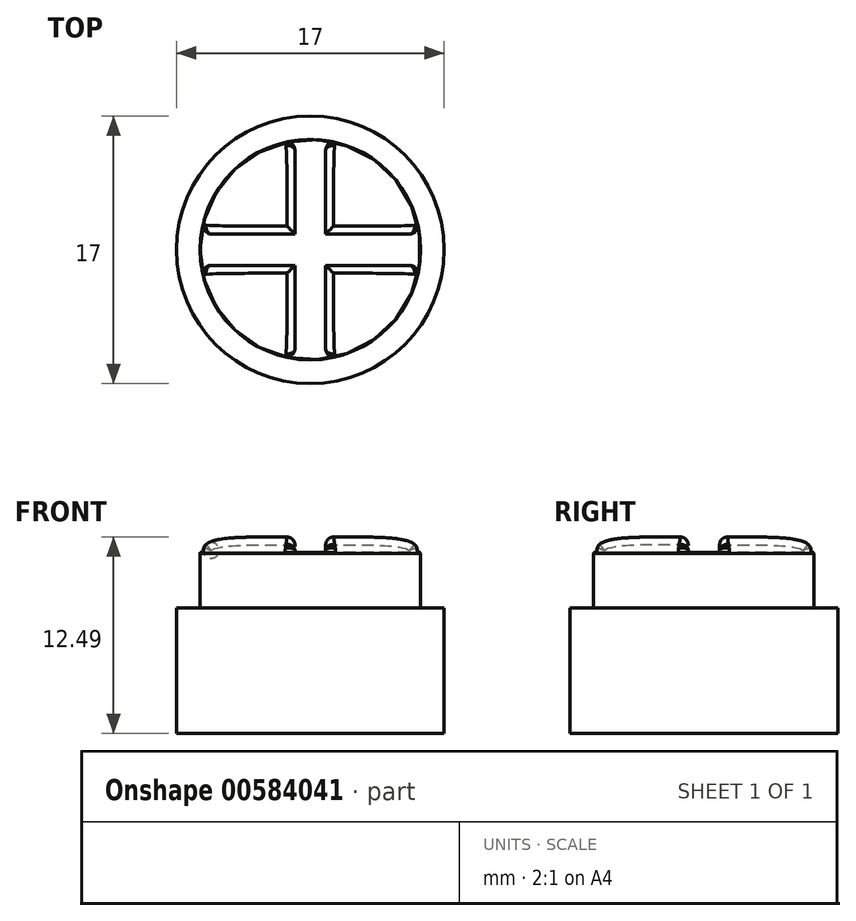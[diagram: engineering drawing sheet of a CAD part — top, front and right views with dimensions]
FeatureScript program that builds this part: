
annotation { "Feature Type Name" : "Feature", "Feature Type Description" : "" }
export const myFeature = defineFeature(function(context is Context, id is Id, definition is map)
    precondition{}
    {
        {
            var Q0;
            Q0=qCreatedBy(makeId("Top.planeOp"),FACE);
            var sketch = newSketch(context, id + "F0", { "sketchPlane" : qUnion([Q0])});
            skCircle(sketch, "E0", {"center": v(0, 0) * mm, "radius": 7 * mm});
            skCircle(sketch, "E1", {"center": v(0, 0) * mm, "radius": 8.5 * mm});
            skSolve(sketch);
        }
        {
            var Q0;
            Q0=makeQuery(id+"F0.imprint","IMPRINT",FACE,{"disambiguationData":[TD([[makeQuery(id+"F0.imprint","IMPRINT",EDGE,{"derivedFrom":sQuery(id+"F0.wireOp",EDGE,"E0")}),1.0]])]});
            extrude(context, id + "F1", {"entities" : qUnion([Q0]), "depth" : 12.5 * mm, "offsetDistance" : 25 * mm});
        }
        {
            var Q0;
            Q0 = qSketchRegion(id + "F0", true);
            extrude(context, id + "F2", {"entities" : qUnion([Q0]), "operationType" : NewBodyOperationType.ADD, "depth" : 8 * mm, "offsetDistance" : 25 * mm});
        }
        {
            var Q0;
            Q0=makeQuery(id+"F1.opExtrude","CAP_FACE",FACE,{"disambiguationData":[OSD([sQuery(id+"F0.wireOp",EDGE,"E0")])],"isStart":false});
            var sketch = newSketch(context, id + "F3", { "sketchPlane" : qUnion([Q0])});
            skLineSegment(sketch, "E2.bottom", {"start": v(7.43, -1) * mm, "end": v(-7.43, -1) * mm});
            skLineSegment(sketch, "E2.top", {"start": v(7.43, 1) * mm, "end": v(-7.43, 1) * mm});
            skLineSegment(sketch, "E2.left", {"start": v(7.43, -1) * mm, "end": v(7.43, 1) * mm});
            skLineSegment(sketch, "E2.right", {"start": v(-7.43, -1) * mm, "end": v(-7.43, 1) * mm});
            skPoint(sketch, "E2.middle", {"position": v(0, 0) * mm});
            skLineSegment(sketch, "E3.bottom", {"start": v(-0.98, 7.33) * mm, "end": v(0.98, 7.33) * mm});
            skLineSegment(sketch, "E3.top", {"start": v(-0.98, -7.33) * mm, "end": v(0.98, -7.33) * mm});
            skLineSegment(sketch, "E3.left", {"start": v(-0.98, 7.33) * mm, "end": v(-0.98, -7.33) * mm});
            skLineSegment(sketch, "E3.right", {"start": v(0.98, 7.33) * mm, "end": v(0.98, -7.33) * mm});
            skSolve(sketch);
        }
        {
            var Q0;
            Q0=qCreatedBy(makeId("Front.planeOp"),FACE);
            var sketch = newSketch(context, id + "F4", { "sketchPlane" : qUnion([Q0])});
            skFitSpline(sketch, "E4", {"points": [v(0, 12.5) * mm, v(-4.49, 12.47) * mm, v(-6.87, 11.94) * mm, v(-6.99, 11.47) * mm, v(-7, 11.43) * mm], "startDerivative": vector(-10.78, -0.52) * mm, "endDerivative": vector(-0.37, -0.56) * mm});
            skFitSpline(sketch, "E5", {"points": [v(-1.66, 12.43) * mm, v(-1.48, 12.47) * mm], "startDerivative": vector(-0.02, 0.02) * mm, "endDerivative": vector(-0.02, 0.02) * mm});
            skLineSegment(sketch, "E6", {"start": v(-7, 11.43) * mm, "end": v(-9.02, 11.43) * mm});
            skLineSegment(sketch, "E7", {"start": v(-9.02, 11.43) * mm, "end": v(-9.02, 13.12) * mm});
            skLineSegment(sketch, "E8", {"start": v(-9.02, 13.12) * mm, "end": v(0, 13.12) * mm});
            skLineSegment(sketch, "E9", {"start": v(0, 13.12) * mm, "end": v(0, 12.5) * mm, "construction": true});
            skLineSegment(sketch, "E10", {"start": v(-9.02, 11.62) * mm, "end": v(0, 11.62) * mm, "construction": true});
            skLineSegment(sketch, "E11", {"start": v(0, 13.12) * mm, "end": v(0, 12.5) * mm});
            skSolve(sketch);
        }
        {
            var Q0;
            Q0=makeQuery(id+"F4.imprint","IMPRINT",FACE,{"disambiguationData":[TD([[makeQuery(id+"F4.imprint","IMPRINT",EDGE,{"derivedFrom":sQuery(id+"F4.wireOp",EDGE,"ac4bd4f6-319e-4e15-baa9-e55c222e8029")}),-1.0]])]});
            var Q1;
            {var subQ0=sQuery(id+"F4.wireOp",EDGE,"E7");Q1=makeQuery(id+"F4.imprint","IMPRINT",FACE,{"disambiguationData":[TD([[makeQuery(id+"F4.imprint","IMPRINT",EDGE,{"derivedFrom":subQ0}),-1.0]])]});}
            var Q2;
            Q2=sQuery(id+"F4.wireOp",EDGE,"E11");
            revolve(context, id + "F5", {"operationType" : NewBodyOperationType.REMOVE, "entities" : qUnion([Q0, Q1]), "axis" : qUnion([Q2]), "revolveType" : RevolveType.FULL, "oppositeDirection" : true});
        }
        {
            var Q0;
            {var subQ0=sQuery(id+"F3.wireOp",EDGE,"bd7cf013-96ed-46fa-b71a-ad90aaa50927.sketch_text.stroke-7");Q0=makeQuery(id+"F3.imprint","IMPRINT",FACE,{"disambiguationData":[TD([[makeQuery(id+"F3.imprint","IMPRINT",EDGE,{"derivedFrom":subQ0}),-1.0]])]});}
            var Q1;
            {var subQ0=sQuery(id+"F3.wireOp",EDGE,"bd7cf013-96ed-46fa-b71a-ad90aaa50927.sketch_text.stroke-1");Q1=makeQuery(id+"F3.imprint","IMPRINT",FACE,{"disambiguationData":[TD([[makeQuery(id+"F3.imprint","IMPRINT",EDGE,{"derivedFrom":subQ0}),-1.0]])]});}
            var Q2;
            {var subQ0=sQuery(id+"F3.wireOp",EDGE,"bd7cf013-96ed-46fa-b71a-ad90aaa50927.sketch_text.stroke-4");Q2=makeQuery(id+"F3.imprint","IMPRINT",FACE,{"disambiguationData":[TD([[makeQuery(id+"F3.imprint","IMPRINT",EDGE,{"derivedFrom":subQ0}),-1.0]])]});}
            var Q3;
            Q3 = qSketchRegion(id + "F3", true);
            extrude(context, id + "F6", {"entities" : qUnion([Q0, Q1, Q2, Q3]), "operationType" : NewBodyOperationType.REMOVE, "oppositeDirection" : true, "depth" : 1 * mm, "offsetDistance" : 25 * mm});
        }
        {
            var Q0;
            {var subQ0=sQuery(id+"F3.wireOp",EDGE,"E2.top");Q0=makeQuery(id+"F6.boolean.opBoolean","INTERSECT",EDGE,{"derivedFrom":[makeQuery(id+"F5.boolean.opBoolean","COPY",FACE,{"derivedFrom":makeQuery(id+"F5.opRevolve","SWEPT_FACE",FACE,{"disambiguationData":[OSD([sQuery(id+"F4.wireOp",EDGE,"E4")])]})}),makeQuery(id+"F6.opExtrude","SWEPT_FACE",FACE,{"disambiguationData":[OSD([subQ0]),TDD([makeQuery(id+"F3.imprint","IMPRINT",EDGE,{"disambiguationData":[TD([[makeQuery(id+"F3.imprint","INTERSECT",VERTEX,{"derivedFrom":[subQ0,sQuery(id+"F3.wireOp",EDGE,"E2.left")]}),-1.0]])],"derivedFrom":subQ0}),makeQuery(id+"F3.imprint","IMPRINT",EDGE,{"disambiguationData":[TD([[makeQuery(id+"F3.imprint","INTERSECT",VERTEX,{"derivedFrom":[subQ0,sQuery(id+"F3.wireOp",EDGE,"E3.right")]}),1.0]])],"derivedFrom":subQ0})])]})]});}
            var Q1;
            {var subQ0=sQuery(id+"F3.wireOp",EDGE,"E2.top");Q1=makeQuery(id+"F6.boolean.opBoolean","INTERSECT",EDGE,{"derivedFrom":[makeQuery(id+"F5.boolean.opBoolean","COPY",FACE,{"derivedFrom":makeQuery(id+"F5.opRevolve","SWEPT_FACE",FACE,{"disambiguationData":[OSD([sQuery(id+"F4.wireOp",EDGE,"E4")])]})}),makeQuery(id+"F6.opExtrude","SWEPT_FACE",FACE,{"disambiguationData":[OSD([subQ0]),TDD([makeQuery(id+"F3.imprint","IMPRINT",EDGE,{"disambiguationData":[TD([[makeQuery(id+"F3.imprint","INTERSECT",VERTEX,{"derivedFrom":[subQ0,sQuery(id+"F3.wireOp",EDGE,"E3.left")]}),-1.0]])],"derivedFrom":subQ0}),makeQuery(id+"F3.imprint","IMPRINT",EDGE,{"disambiguationData":[TD([[makeQuery(id+"F3.imprint","INTERSECT",VERTEX,{"derivedFrom":[subQ0,sQuery(id+"F3.wireOp",EDGE,"E2.right")]}),1.0]])],"derivedFrom":subQ0})])]})]});}
            var Q2;
            {var subQ0=sQuery(id+"F3.wireOp",EDGE,"E3.left");Q2=makeQuery(id+"F6.boolean.opBoolean","INTERSECT",EDGE,{"derivedFrom":[makeQuery(id+"F5.boolean.opBoolean","COPY",FACE,{"derivedFrom":makeQuery(id+"F5.opRevolve","SWEPT_FACE",FACE,{"disambiguationData":[OSD([sQuery(id+"F4.wireOp",EDGE,"E4")])]})}),makeQuery(id+"F6.opExtrude","SWEPT_FACE",FACE,{"disambiguationData":[OSD([subQ0]),TDD([makeQuery(id+"F3.imprint","IMPRINT",EDGE,{"disambiguationData":[TD([[makeQuery(id+"F3.imprint","INTERSECT",VERTEX,{"derivedFrom":[sQuery(id+"F3.wireOp",EDGE,"E2.bottom"),subQ0]}),-1.0]])],"derivedFrom":subQ0}),makeQuery(id+"F3.imprint","IMPRINT",EDGE,{"disambiguationData":[TD([[makeQuery(id+"F3.imprint","INTERSECT",VERTEX,{"derivedFrom":[sQuery(id+"F3.wireOp",EDGE,"E3.top"),subQ0]}),1.0]])],"derivedFrom":subQ0})])]})]});}
            var Q3;
            {var subQ0=sQuery(id+"F3.wireOp",EDGE,"E3.left");Q3=makeQuery(id+"F6.boolean.opBoolean","INTERSECT",EDGE,{"derivedFrom":[makeQuery(id+"F5.boolean.opBoolean","COPY",FACE,{"derivedFrom":makeQuery(id+"F5.opRevolve","SWEPT_FACE",FACE,{"disambiguationData":[OSD([sQuery(id+"F4.wireOp",EDGE,"E4")])]})}),makeQuery(id+"F6.opExtrude","SWEPT_FACE",FACE,{"disambiguationData":[OSD([subQ0]),TDD([makeQuery(id+"F3.imprint","IMPRINT",EDGE,{"disambiguationData":[TD([[makeQuery(id+"F3.imprint","INTERSECT",VERTEX,{"derivedFrom":[sQuery(id+"F3.wireOp",EDGE,"E3.bottom"),subQ0]}),-1.0]])],"derivedFrom":subQ0}),makeQuery(id+"F3.imprint","IMPRINT",EDGE,{"disambiguationData":[TD([[makeQuery(id+"F3.imprint","INTERSECT",VERTEX,{"derivedFrom":[sQuery(id+"F3.wireOp",EDGE,"E2.top"),subQ0]}),1.0]])],"derivedFrom":subQ0})])]})]});}
            var Q4;
            {var subQ0=sQuery(id+"F3.wireOp",EDGE,"E3.right");Q4=makeQuery(id+"F6.boolean.opBoolean","INTERSECT",EDGE,{"derivedFrom":[makeQuery(id+"F5.boolean.opBoolean","COPY",FACE,{"derivedFrom":makeQuery(id+"F5.opRevolve","SWEPT_FACE",FACE,{"disambiguationData":[OSD([sQuery(id+"F4.wireOp",EDGE,"E4")])]})}),makeQuery(id+"F6.opExtrude","SWEPT_FACE",FACE,{"disambiguationData":[OSD([subQ0]),TDD([makeQuery(id+"F3.imprint","IMPRINT",EDGE,{"disambiguationData":[TD([[makeQuery(id+"F3.imprint","INTERSECT",VERTEX,{"derivedFrom":[sQuery(id+"F3.wireOp",EDGE,"E2.bottom"),subQ0]}),-1.0]])],"derivedFrom":subQ0}),makeQuery(id+"F3.imprint","IMPRINT",EDGE,{"disambiguationData":[TD([[makeQuery(id+"F3.imprint","INTERSECT",VERTEX,{"derivedFrom":[sQuery(id+"F3.wireOp",EDGE,"E3.top"),subQ0]}),1.0]])],"derivedFrom":subQ0})])]})]});}
            var Q5;
            {var subQ0=sQuery(id+"F3.wireOp",EDGE,"E3.right");Q5=makeQuery(id+"F6.boolean.opBoolean","INTERSECT",EDGE,{"derivedFrom":[makeQuery(id+"F5.boolean.opBoolean","COPY",FACE,{"derivedFrom":makeQuery(id+"F5.opRevolve","SWEPT_FACE",FACE,{"disambiguationData":[OSD([sQuery(id+"F4.wireOp",EDGE,"E4")])]})}),makeQuery(id+"F6.opExtrude","SWEPT_FACE",FACE,{"disambiguationData":[OSD([subQ0]),TDD([makeQuery(id+"F3.imprint","IMPRINT",EDGE,{"disambiguationData":[TD([[makeQuery(id+"F3.imprint","INTERSECT",VERTEX,{"derivedFrom":[sQuery(id+"F3.wireOp",EDGE,"E3.bottom"),subQ0]}),-1.0]])],"derivedFrom":subQ0}),makeQuery(id+"F3.imprint","IMPRINT",EDGE,{"disambiguationData":[TD([[makeQuery(id+"F3.imprint","INTERSECT",VERTEX,{"derivedFrom":[sQuery(id+"F3.wireOp",EDGE,"E2.top"),subQ0]}),1.0]])],"derivedFrom":subQ0})])]})]});}
            var Q6;
            {var subQ0=sQuery(id+"F3.wireOp",EDGE,"E2.bottom");Q6=makeQuery(id+"F6.boolean.opBoolean","INTERSECT",EDGE,{"derivedFrom":[makeQuery(id+"F5.boolean.opBoolean","COPY",FACE,{"derivedFrom":makeQuery(id+"F5.opRevolve","SWEPT_FACE",FACE,{"disambiguationData":[OSD([sQuery(id+"F4.wireOp",EDGE,"E4")])]})}),makeQuery(id+"F6.opExtrude","SWEPT_FACE",FACE,{"disambiguationData":[OSD([subQ0]),TDD([makeQuery(id+"F3.imprint","IMPRINT",EDGE,{"disambiguationData":[TD([[makeQuery(id+"F3.imprint","INTERSECT",VERTEX,{"derivedFrom":[subQ0,sQuery(id+"F3.wireOp",EDGE,"E3.left")]}),-1.0]])],"derivedFrom":subQ0}),makeQuery(id+"F3.imprint","IMPRINT",EDGE,{"disambiguationData":[TD([[makeQuery(id+"F3.imprint","INTERSECT",VERTEX,{"derivedFrom":[subQ0,sQuery(id+"F3.wireOp",EDGE,"E2.right")]}),1.0]])],"derivedFrom":subQ0})])]})]});}
            var Q7;
            {var subQ0=sQuery(id+"F3.wireOp",EDGE,"E2.bottom");Q7=makeQuery(id+"F6.boolean.opBoolean","INTERSECT",EDGE,{"derivedFrom":[makeQuery(id+"F5.boolean.opBoolean","COPY",FACE,{"derivedFrom":makeQuery(id+"F5.opRevolve","SWEPT_FACE",FACE,{"disambiguationData":[OSD([sQuery(id+"F4.wireOp",EDGE,"E4")])]})}),makeQuery(id+"F6.opExtrude","SWEPT_FACE",FACE,{"disambiguationData":[OSD([subQ0]),TDD([makeQuery(id+"F3.imprint","IMPRINT",EDGE,{"disambiguationData":[TD([[makeQuery(id+"F3.imprint","INTERSECT",VERTEX,{"derivedFrom":[subQ0,sQuery(id+"F3.wireOp",EDGE,"E2.left")]}),-1.0]])],"derivedFrom":subQ0}),makeQuery(id+"F3.imprint","IMPRINT",EDGE,{"disambiguationData":[TD([[makeQuery(id+"F3.imprint","INTERSECT",VERTEX,{"derivedFrom":[subQ0,sQuery(id+"F3.wireOp",EDGE,"E3.right")]}),1.0]])],"derivedFrom":subQ0})])]})]});}
            fillet(context, id + "F7", {"entities" : qUnion([Q0, Q1, Q2, Q3, Q4, Q5, Q6, Q7]), "radius" : .5 * mm, "tangentPropagation" : true, "allowEdgeOverflow" : false});
        }
    });
